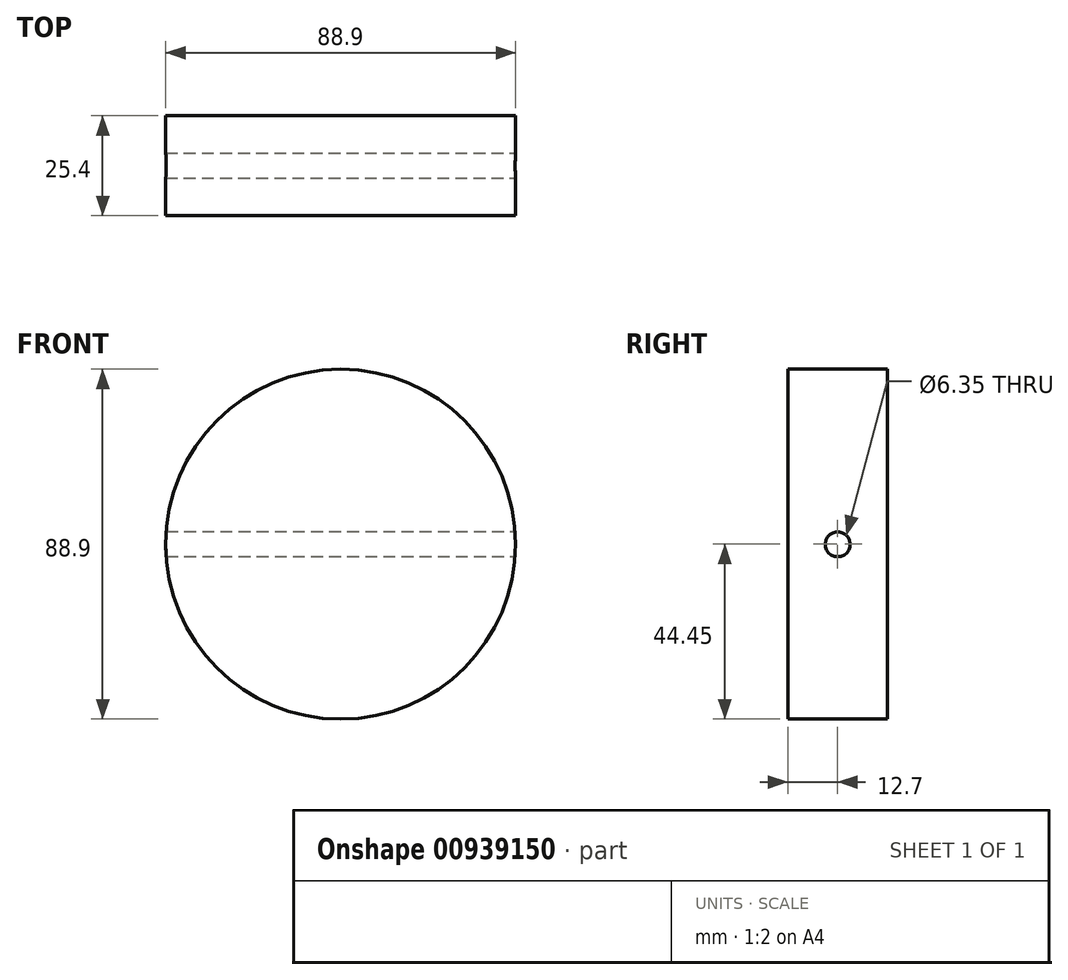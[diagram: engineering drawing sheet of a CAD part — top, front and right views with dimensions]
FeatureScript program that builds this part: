
annotation { "Feature Type Name" : "Feature", "Feature Type Description" : "" }
export const myFeature = defineFeature(function(context is Context, id is Id, definition is map)
    precondition{}
    {
        {
            var Q0;
            Q0=qCreatedBy(makeId("Front.planeOp"),FACE);
            var sketch = newSketch(context, id + "F0", { "sketchPlane" : qUnion([Q0])});
            skCircle(sketch, "E0", {"center": v(0, 0) * mm, "radius": 44.45 * mm});
            skSolve(sketch);
        }
        {
            var Q0;
            Q0=makeQuery(id+"F0.imprint","IMPRINT",FACE,{"disambiguationData":[TD([[makeQuery(id+"F0.imprint","IMPRINT",EDGE,{"derivedFrom":sQuery(id+"F0.wireOp",EDGE,"E0")}),1.0]])]});
            extrude(context, id + "F1", {"entities" : qUnion([Q0]), "endBound" : BoundingType.SYMMETRIC, "depth" : 25.4 * mm, "offsetDistance" : 25.4 * mm});
        }
        {
            var Q0;
            Q0=qCreatedBy(makeId("Right.planeOp"),FACE);
            cPlane(context, id + "F2", {"entities" : qUnion([Q0]), "cplaneType" : CPlaneType.OFFSET, "offset" : 44.45 * mm, "width" : 152.4 * mm, "height" : 152.4 * mm});
        }
        {
            var Q0;
            Q0=qCreatedBy(id+"F2.planeOp",FACE);
            var sketch = newSketch(context, id + "F3", { "sketchPlane" : qUnion([Q0])});
            skPoint(sketch, "E1", {"position": v(0, 0) * mm});
            skSolve(sketch);
        }
        {
            var Q0;
            Q0=sQuery(id+"F3.wireOp",VERTEX,"E1");
            var Q1;
            Q1=makeQuery(id+"F1.opExtrude","SWEPT_BODY",BODY,{"disambiguationData":[OSD([sQuery(id+"F0.wireOp",EDGE,"E0")])]});
            hole(context, id + "F4", {"style" : HoleStyle.SIMPLE, "endStyle" : HoleEndStyle.THROUGH, "holeDiameter" : 6.35 * mm, "majorDiameter" : 6.35 * mm, "isTappedThrough" : true, "tappedDepth" : 12.7 * mm, "tapClearance" : 3, "locations" : qUnion([Q0]), "scope" : qUnion([Q1])});
        }
    });
